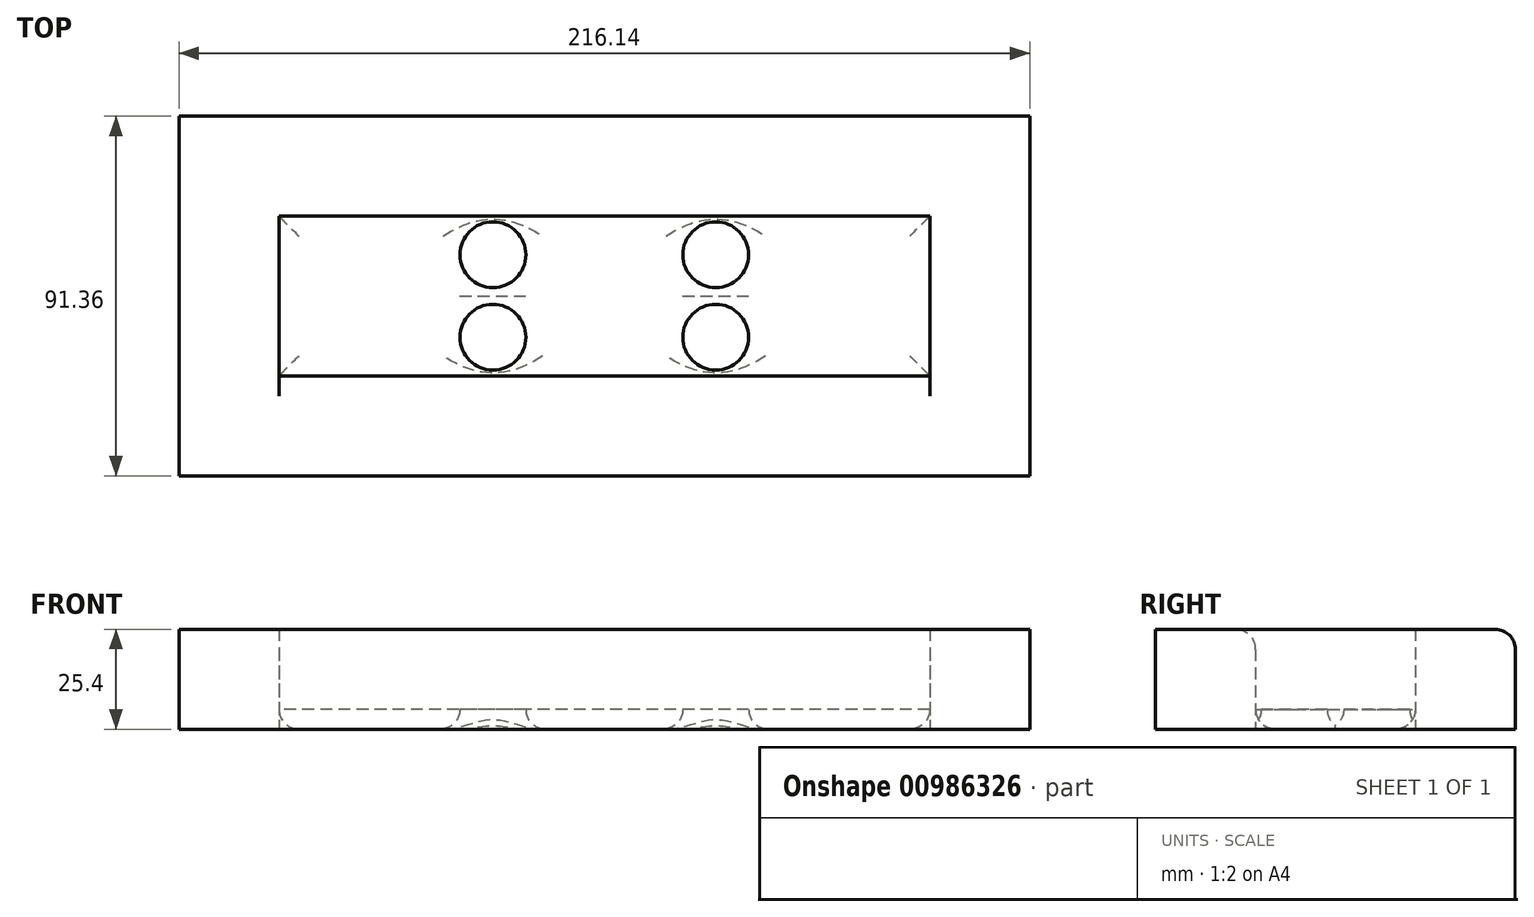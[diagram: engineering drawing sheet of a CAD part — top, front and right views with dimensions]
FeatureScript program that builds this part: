
annotation { "Feature Type Name" : "Feature", "Feature Type Description" : "" }
export const myFeature = defineFeature(function(context is Context, id is Id, definition is map)
    precondition{}
    {
        {
            var Q0;
            Q0=qCreatedBy(makeId("Top.planeOp"),FACE);
            var sketch = newSketch(context, id + "F0", { "sketchPlane" : qUnion([Q0])});
            skLineSegment(sketch, "E0.bottom", {"start": v(82.67, -20.28) * mm, "end": v(-82.67, -20.28) * mm});
            skLineSegment(sketch, "E0.top", {"start": v(82.67, 20.28) * mm, "end": v(-82.67, 20.28) * mm});
            skLineSegment(sketch, "E0.left", {"start": v(82.67, -20.28) * mm, "end": v(82.67, 20.28) * mm});
            skLineSegment(sketch, "E0.right", {"start": v(-82.67, -20.28) * mm, "end": v(-82.67, 20.28) * mm});
            skPoint(sketch, "E0.middle", {"position": v(0, 0) * mm});
            skLineSegment(sketch, "E1.0", {"start": v(108.07, 45.68) * mm, "end": v(-108.07, 45.68) * mm});
            skLineSegment(sketch, "E1.1", {"start": v(108.07, -45.68) * mm, "end": v(108.07, 45.68) * mm});
            skLineSegment(sketch, "E1.2", {"start": v(108.07, -45.68) * mm, "end": v(-108.07, -45.68) * mm});
            skLineSegment(sketch, "E1.3", {"start": v(-108.07, -45.68) * mm, "end": v(-108.07, 45.68) * mm});
            skLineSegment(sketch, "E2.bottom", {"start": v(-28.3, 10.48) * mm, "end": v(28.3, 10.48) * mm, "construction": true});
            skLineSegment(sketch, "E2.top", {"start": v(-28.3, -10.48) * mm, "end": v(28.3, -10.48) * mm, "construction": true});
            skLineSegment(sketch, "E2.left", {"start": v(-28.3, 10.48) * mm, "end": v(-28.3, -10.48) * mm, "construction": true});
            skLineSegment(sketch, "E2.right", {"start": v(28.3, 10.48) * mm, "end": v(28.3, -10.48) * mm, "construction": true});
            skCircle(sketch, "E3", {"center": v(-28.3, 10.48) * mm, "radius": 8.38 * mm});
            skCircle(sketch, "E4", {"center": v(28.3, 10.48) * mm, "radius": 8.38 * mm});
            skCircle(sketch, "E5", {"center": v(-28.3, -10.48) * mm, "radius": 8.38 * mm});
            skCircle(sketch, "E6", {"center": v(28.3, -10.48) * mm, "radius": 8.38 * mm});
            skSolve(sketch);
        }
        {
            var Q0;
            Q0=makeQuery(id+"F0.imprint","IMPRINT",FACE,{"disambiguationData":[TD([[makeQuery(id+"F0.imprint","IMPRINT",EDGE,{"derivedFrom":sQuery(id+"F0.wireOp",EDGE,"E0.bottom")}),1.0]])]});
            extrude(context, id + "F1", {"entities" : qUnion([Q0]), "depth" : 25.4 * mm, "offsetDistance" : 25.4 * mm});
        }
        {
            var Q0;
            Q0=makeQuery(id+"F0.imprint","IMPRINT",FACE,{"disambiguationData":[TD([[makeQuery(id+"F0.imprint","IMPRINT",EDGE,{"derivedFrom":sQuery(id+"F0.wireOp",EDGE,"E0.bottom")}),-1.0]])]});
            extrude(context, id + "F2", {"entities" : qUnion([Q0]), "depth" : 5.08 * mm, "offsetDistance" : 25.4 * mm});
        }
        {
            var Q0;
            Q0=makeQuery(id+"F2.opExtrude","CAP_FACE",FACE,{"disambiguationData":[OSD([sQuery(id+"F0.wireOp",EDGE,"E0.bottom"),sQuery(id+"F0.wireOp",EDGE,"E0.top"),sQuery(id+"F0.wireOp",EDGE,"E0.left"),sQuery(id+"F0.wireOp",EDGE,"E0.right"),sQuery(id+"F0.wireOp",EDGE,"E3"),sQuery(id+"F0.wireOp",EDGE,"E4"),sQuery(id+"F0.wireOp",EDGE,"E5"),sQuery(id+"F0.wireOp",EDGE,"E6")])],"isStart":true});
            var Q1;
            Q1=makeQuery(id+"F1.opExtrude","CAP_EDGE",EDGE,{"disambiguationData":[OSD([sQuery(id+"F0.wireOp",EDGE,"E1.0")])],"isStart":false});
            var Q2;
            Q2=makeQuery(id+"F1.opExtrude","CAP_EDGE",EDGE,{"disambiguationData":[OSD([sQuery(id+"F0.wireOp",EDGE,"E0.bottom")])],"isStart":false});
            fillet(context, id + "F3", {"entities" : qUnion([Q0, Q1, Q2]), "radius" : 5.08 * mm, "tangentPropagation" : true, "allowEdgeOverflow" : false});
        }
    });
